FCSTD DOCUMENT  (FreeCAD 1.1R41365 (Git))
Label: MicroManipulatorAssembly
License: All rights reserved
LicenseURL: https://en.wikipedia.org/wiki/All_rights_reserved
objects: App::Link×31, Assembly::AssemblyLink×7, App::Point×5, Assembly::JointGroup×1, Assembly::AssemblyObject×1
EXTERNAL_REF file=ActuatorAssembly.FCStd obj=Assembly
EXTERNAL_REF file=ActuatorAssembly.FCStd obj=FlexureStageBase
EXTERNAL_REF file=ActuatorAssembly.FCStd obj=FlexureStage
EXTERNAL_REF file=EndEffectorAssembly.FCStd obj=Assembly
EXTERNAL_REF file=EndEffectorAssembly.FCStd obj=Endeffector
EXTERNAL_REF file=ActuatorAssembly.FCStd obj=LeadscrewWheel
EXTERNAL_REF file=ActuatorAssembly.FCStd obj=FlexureAssembly
EXTERNAL_REF file=FlexureAssembly.FCStd obj=WireMount
EXTERNAL_REF file=FlexureAssembly.FCStd obj=WireMount001
EXTERNAL_REF file=FlexureAssembly.FCStd obj=FlexureWire
EXTERNAL_REF file=FlexureAssembly.FCStd obj=FlexureWire001
EXTERNAL_REF file=FlexureAssembly.FCStd obj=Rod
EXTERNAL_REF file=FlexureAssembly.FCStd obj=FlexureStiffener
EXTERNAL_REF file=FlexureAssembly.FCStd obj=WireMountFixture

FEATURE [App::Point] Origin001
  Role = Origin
FEATURE [Assembly::JointGroup] Joints
FEATURE [App::Point] Origin003
  Role = Origin
FEATURE [App::Link] FlexureStageBase
  LinkPlacement = pos=(3.75918e-06,-42.5,2) rot=(0,0,1;3.14159rad)
  LinkedObject = -> <external ActuatorAssembly.FCStd>#FlexureStageBase
  Placement = pos=(3.75918e-06,-42.5,2) rot=(0,0,1;3.14159rad)
FEATURE [App::Link] FlexureStage
  LinkPlacement = pos=(0,-19,19) rot=(0,1,0;3.14159rad)
  LinkedObject = -> <external ActuatorAssembly.FCStd>#FlexureStage
  Placement = pos=(0,-19,19) rot=(0,1,0;3.14159rad)
FEATURE [App::Point] Origin005
  Role = Origin
FEATURE [App::Link] FlexureStageBase001
  LinkPlacement = pos=(3.75918e-06,-42.5,2) rot=(0,0,1;3.14159rad)
  LinkedObject = -> <external ActuatorAssembly.FCStd>#FlexureStageBase
  Placement = pos=(3.75918e-06,-42.5,2) rot=(0,0,1;3.14159rad)
FEATURE [App::Link] FlexureStage001
  LinkPlacement = pos=(0,-19,19) rot=(0,1,0;3.14159rad)
  LinkedObject = -> <external ActuatorAssembly.FCStd>#FlexureStage
  Placement = pos=(0,-19,19) rot=(0,1,0;3.14159rad)
FEATURE [App::Point] Origin007
  Role = Origin
FEATURE [App::Link] FlexureStageBase002
  LinkPlacement = pos=(3.75918e-06,-42.5,2) rot=(0,0,1;3.14159rad)
  LinkedObject = -> <external ActuatorAssembly.FCStd>#FlexureStageBase
  Placement = pos=(3.75918e-06,-42.5,2) rot=(0,0,1;3.14159rad)
FEATURE [App::Link] FlexureStage002
  LinkPlacement = pos=(0,-19,19) rot=(0,1,0;3.14159rad)
  LinkedObject = -> <external ActuatorAssembly.FCStd>#FlexureStage
  Placement = pos=(0,-19,19) rot=(0,1,0;3.14159rad)
FEATURE [App::Point] Origin009
  Role = Origin
FEATURE [App::Link] Endeffector
  LinkedObject = -> <external EndEffectorAssembly.FCStd>#Endeffector
FEATURE [Assembly::AssemblyLink] EndEffectorAssembly
  Group = -> [Endeffector]
  LinkedObject = -> <external EndEffectorAssembly.FCStd>#Assembly
  Origin = -> Origin008
  Placement = pos=(0,0,0) rot=(0,0,1;1.5708rad)
  Rigid = true
FEATURE [App::Link] LeadscrewWheel
  LinkPlacement = pos=(23,-13,13) rot=(0,1,0;1.5708rad)
  LinkedObject = -> <external ActuatorAssembly.FCStd>#LeadscrewWheel
  Placement = pos=(23,-13,13) rot=(0,1,0;1.5708rad)
FEATURE [App::Link] LeadscrewWheel001
  LinkPlacement = pos=(23,-13,13) rot=(0,1,0;1.5708rad)
  LinkedObject = -> <external ActuatorAssembly.FCStd>#LeadscrewWheel
  Placement = pos=(23,-13,13) rot=(0,1,0;1.5708rad)
FEATURE [App::Link] LeadscrewWheel002
  LinkPlacement = pos=(23,-13,13) rot=(0,1,0;1.5708rad)
  LinkedObject = -> <external ActuatorAssembly.FCStd>#LeadscrewWheel
  Placement = pos=(23,-13,13) rot=(0,1,0;1.5708rad)
FEATURE [App::Link] WireMount006
  LinkedObject = -> <external FlexureAssembly.FCStd>#WireMount
FEATURE [App::Link] WireMount007
  LinkPlacement = pos=(0,-55,3) rot=(1,0,0;3.14159rad)
  LinkedObject = -> <external FlexureAssembly.FCStd>#WireMount001
  Placement = pos=(0,-55,3) rot=(1,0,0;3.14159rad)
FEATURE [App::Link] FlexureWire006
  LinkPlacement = pos=(8,3.5,1.5) rot=(0,0,1;0rad)
  LinkedObject = -> <external FlexureAssembly.FCStd>#FlexureWire
  Placement = pos=(8,3.5,1.5) rot=(0,0,1;0rad)
FEATURE [App::Link] FlexureWire007
  LinkPlacement = pos=(-8.00001,3.5,1.5) rot=(0,0,1;0rad)
  LinkedObject = -> <external FlexureAssembly.FCStd>#FlexureWire001
  Placement = pos=(-8.00001,3.5,1.5) rot=(0,0,1;0rad)
FEATURE [App::Link] Rod003  label="FlexureStiffener003"
  LinkPlacement = pos=(-8,-27.5,1.5) rot=(0,0,1;0rad)
  LinkedObject = -> <external FlexureAssembly.FCStd>#Rod
  Placement = pos=(-8,-27.5,1.5) rot=(0,0,1;0rad)
FEATURE [App::Link] FlexureStiffener003
  LinkPlacement = pos=(8,-27.5,1.5) rot=(0,0,1;0rad)
  LinkedObject = -> <external FlexureAssembly.FCStd>#FlexureStiffener
  Placement = pos=(8,-27.5,1.5) rot=(0,0,1;0rad)
FEATURE [App::Link] WireMountFixture003
  LinkPlacement = pos=(0,-27.5,-5) rot=(0,0,1;0rad)
  LinkedObject = -> <external FlexureAssembly.FCStd>#WireMountFixture
  Placement = pos=(0,-27.5,-5) rot=(0,0,1;0rad)
FEATURE [Assembly::AssemblyLink] FlexureAssembly003  label="FlexureAssembly"
  Group = -> [WireMount006,WireMount007,FlexureWire006,FlexureWire007,Rod003,FlexureStiffener003,WireMountFixture003]
  LinkedObject = -> <external ActuatorAssembly.FCStd>#FlexureAssembly
  Placement = pos=(-54.5,-13,19) rot=(0,0,1;1.5708rad)
  Rigid = true
FEATURE [Assembly::AssemblyLink] ActuatorAssembly  label="ActuatorAssembly1"
  Group = -> [FlexureStageBase,FlexureStage,LeadscrewWheel,FlexureAssembly003]
  LinkedObject = -> <external ActuatorAssembly.FCStd>#Assembly
  Origin = -> Origin002
  Placement = pos=(51.5,14.5,-33.5) rot=(-0.660516,-0.330258,0.674276;0rad)
  Rigid = true
FEATURE [App::Link] WireMount008
  LinkedObject = -> <external FlexureAssembly.FCStd>#WireMount
FEATURE [App::Link] WireMount009
  LinkPlacement = pos=(0,-55,3) rot=(1,0,0;3.14159rad)
  LinkedObject = -> <external FlexureAssembly.FCStd>#WireMount001
  Placement = pos=(0,-55,3) rot=(1,0,0;3.14159rad)
FEATURE [App::Link] FlexureWire008
  LinkPlacement = pos=(8,3.5,1.5) rot=(0,0,1;0rad)
  LinkedObject = -> <external FlexureAssembly.FCStd>#FlexureWire
  Placement = pos=(8,3.5,1.5) rot=(0,0,1;0rad)
FEATURE [App::Link] FlexureWire009
  LinkPlacement = pos=(-8.00001,3.5,1.5) rot=(0,0,1;0rad)
  LinkedObject = -> <external FlexureAssembly.FCStd>#FlexureWire001
  Placement = pos=(-8.00001,3.5,1.5) rot=(0,0,1;0rad)
FEATURE [App::Link] Rod004  label="FlexureStiffener004"
  LinkPlacement = pos=(-8,-27.5,1.5) rot=(0,0,1;0rad)
  LinkedObject = -> <external FlexureAssembly.FCStd>#Rod
  Placement = pos=(-8,-27.5,1.5) rot=(0,0,1;0rad)
FEATURE [App::Link] FlexureStiffener004
  LinkPlacement = pos=(8,-27.5,1.5) rot=(0,0,1;0rad)
  LinkedObject = -> <external FlexureAssembly.FCStd>#FlexureStiffener
  Placement = pos=(8,-27.5,1.5) rot=(0,0,1;0rad)
FEATURE [App::Link] WireMountFixture004
  LinkPlacement = pos=(0,-27.5,-5) rot=(0,0,1;0rad)
  LinkedObject = -> <external FlexureAssembly.FCStd>#WireMountFixture
  Placement = pos=(0,-27.5,-5) rot=(0,0,1;0rad)
FEATURE [Assembly::AssemblyLink] FlexureAssembly004
  Group = -> [WireMount008,WireMount009,FlexureWire008,FlexureWire009,Rod004,FlexureStiffener004,WireMountFixture004]
  LinkedObject = -> <external ActuatorAssembly.FCStd>#FlexureAssembly
  Placement = pos=(-54.5,-13,19) rot=(0,0,1;1.5708rad)
  Rigid = true
FEATURE [Assembly::AssemblyLink] ActuatorAssembly001  label="ActuatorAssembly2"
  Group = -> [FlexureStageBase001,FlexureStage001,LeadscrewWheel001,FlexureAssembly004]
  LinkedObject = -> <external ActuatorAssembly.FCStd>#Assembly
  Origin = -> Origin004
  Placement = pos=(33.5,-51.5,14.5) rot=(-0.57735,0.57735,0.57735;4.18879rad)
  Rigid = true
FEATURE [App::Link] WireMount010
  LinkedObject = -> <external FlexureAssembly.FCStd>#WireMount
FEATURE [App::Link] WireMount011
  LinkPlacement = pos=(0,-55,3) rot=(1,0,0;3.14159rad)
  LinkedObject = -> <external FlexureAssembly.FCStd>#WireMount001
  Placement = pos=(0,-55,3) rot=(1,0,0;3.14159rad)
FEATURE [App::Link] FlexureWire010
  LinkPlacement = pos=(8,3.5,1.5) rot=(0,0,1;0rad)
  LinkedObject = -> <external FlexureAssembly.FCStd>#FlexureWire
  Placement = pos=(8,3.5,1.5) rot=(0,0,1;0rad)
FEATURE [App::Link] FlexureWire011
  LinkPlacement = pos=(-8.00001,3.5,1.5) rot=(0,0,1;0rad)
  LinkedObject = -> <external FlexureAssembly.FCStd>#FlexureWire001
  Placement = pos=(-8.00001,3.5,1.5) rot=(0,0,1;0rad)
FEATURE [App::Link] Rod005  label="FlexureStiffener005"
  LinkPlacement = pos=(-8,-27.5,1.5) rot=(0,0,1;0rad)
  LinkedObject = -> <external FlexureAssembly.FCStd>#Rod
  Placement = pos=(-8,-27.5,1.5) rot=(0,0,1;0rad)
FEATURE [App::Link] FlexureStiffener005
  LinkPlacement = pos=(8,-27.5,1.5) rot=(0,0,1;0rad)
  LinkedObject = -> <external FlexureAssembly.FCStd>#FlexureStiffener
  Placement = pos=(8,-27.5,1.5) rot=(0,0,1;0rad)
FEATURE [App::Link] WireMountFixture005
  LinkPlacement = pos=(0,-27.5,-5) rot=(0,0,1;0rad)
  LinkedObject = -> <external FlexureAssembly.FCStd>#WireMountFixture
  Placement = pos=(0,-27.5,-5) rot=(0,0,1;0rad)
FEATURE [Assembly::AssemblyLink] FlexureAssembly005
  Group = -> [WireMount010,WireMount011,FlexureWire010,FlexureWire011,Rod005,FlexureStiffener005,WireMountFixture005]
  LinkedObject = -> <external ActuatorAssembly.FCStd>#FlexureAssembly
  Placement = pos=(-54.5,-13,19) rot=(0,0,1;1.5708rad)
  Rigid = true
FEATURE [Assembly::AssemblyLink] ActuatorAssembly002  label="ActuatorAssembly3"
  Group = -> [FlexureStageBase002,FlexureStage002,LeadscrewWheel002,FlexureAssembly005]
  LinkedObject = -> <external ActuatorAssembly.FCStd>#Assembly
  Origin = -> Origin006
  Placement = pos=(-14.5,-33.5,-51.5) rot=(-0.57735,0.57735,0.57735;2.0944rad)
  Rigid = true
FEATURE [Assembly::AssemblyObject] Assembly  label="MicroManipulator"
  Group = -> [Joints,ActuatorAssembly,ActuatorAssembly001,ActuatorAssembly002,EndEffectorAssembly]
  Origin = -> Origin
  Type = Assembly

RESOLVED EXTERNAL PARTS (link-assembly join: the EXTERNAL_REF files above that resolve inside this repo's crawl, each included once):
---- part ActuatorAssembly.FCStd = doc fcstd_1e1ebc22bf72 ----
FCSTD DOCUMENT  (FreeCAD 1.1R41365 (Git))
Label: ActuatorAssembly
License: All rights reserved
LicenseURL: https://en.wikipedia.org/wiki/All_rights_reserved
objects: App::Link×10, App::Point×2, App::FeaturePython×1, Assembly::JointGroup×1, Assembly::AssemblyLink×1, Assembly::AssemblyObject×1
EXTERNAL_REF file=FlexureStageBase.FCStd obj=Body
EXTERNAL_REF file=FlexureStage.FCStd obj=Body
EXTERNAL_REF file=LeadscrewWheel.FCStd obj=Body
EXTERNAL_REF file=FlexureAssembly.FCStd obj=Assembly
EXTERNAL_REF file=FlexureAssembly.FCStd obj=WireMount
EXTERNAL_REF file=FlexureAssembly.FCStd obj=WireMount001
EXTERNAL_REF file=FlexureAssembly.FCStd obj=FlexureWire
EXTERNAL_REF file=FlexureAssembly.FCStd obj=FlexureWire001
EXTERNAL_REF file=FlexureAssembly.FCStd obj=Rod
EXTERNAL_REF file=FlexureAssembly.FCStd obj=FlexureStiffener
EXTERNAL_REF file=FlexureAssembly.FCStd obj=WireMountFixture

FEATURE [App::Point] Origin001
  Role = Origin
FEATURE [App::Link] FlexureStageBase
  LinkPlacement = pos=(3.75918e-06,-42.5,2) rot=(0,0,1;3.14159rad)
  LinkedObject = -> <external FlexureStageBase.FCStd>#Body
  Placement = pos=(3.75918e-06,-42.5,2) rot=(0,0,1;3.14159rad)
FEATURE [App::Link] FlexureStage
  LinkPlacement = pos=(0,-19,19) rot=(0,1,0;3.14159rad)
  LinkedObject = -> <external FlexureStage.FCStd>#Body
  Placement = pos=(0,-19,19) rot=(0,1,0;3.14159rad)
FEATURE [App::Link] LeadscrewWheel
  LinkPlacement = pos=(23,-13,13) rot=(0,1,0;1.5708rad)
  LinkedObject = -> <external LeadscrewWheel.FCStd>#Body
  Placement = pos=(23,-13,13) rot=(0,1,0;1.5708rad)
FEATURE [App::FeaturePython] GroundedJoint  # Assembly grounded joint (typed FeaturePython)
  ObjectToGround = -> LeadscrewWheel
FEATURE [Assembly::JointGroup] Joints
  Group = -> [GroundedJoint]
FEATURE [App::Point] Origin003
  Role = Origin
FEATURE [App::Link] WireMount  label="WireMount1"
  LinkedObject = -> <external FlexureAssembly.FCStd>#WireMount
FEATURE [App::Link] WireMount001  label="WireMount2"
  LinkPlacement = pos=(0,-55,3) rot=(1,0,0;3.14159rad)
  LinkedObject = -> <external FlexureAssembly.FCStd>#WireMount001
  Placement = pos=(0,-55,3) rot=(1,0,0;3.14159rad)
FEATURE [App::Link] FlexureWire  label="FlexureWire1"
  LinkPlacement = pos=(8,3.5,1.5) rot=(0,0,1;0rad)
  LinkedObject = -> <external FlexureAssembly.FCStd>#FlexureWire
  Placement = pos=(8,3.5,1.5) rot=(0,0,1;0rad)
FEATURE [App::Link] FlexureWire001  label="FlexureWire2"
  LinkPlacement = pos=(-8.00001,3.5,1.5) rot=(0,0,1;0rad)
  LinkedObject = -> <external FlexureAssembly.FCStd>#FlexureWire001
  Placement = pos=(-8.00001,3.5,1.5) rot=(0,0,1;0rad)
FEATURE [App::Link] Rod  label="FlexureStiffener1"
  LinkPlacement = pos=(-8,-27.5,1.5) rot=(0,0,1;0rad)
  LinkedObject = -> <external FlexureAssembly.FCStd>#Rod
  Placement = pos=(-8,-27.5,1.5) rot=(0,0,1;0rad)
FEATURE [App::Link] FlexureStiffener  label="FlexureStiffener2"
  LinkPlacement = pos=(8,-27.5,1.5) rot=(0,0,1;0rad)
  LinkedObject = -> <external FlexureAssembly.FCStd>#FlexureStiffener
  Placement = pos=(8,-27.5,1.5) rot=(0,0,1;0rad)
FEATURE [App::Link] WireMountFixture
  LinkPlacement = pos=(0,-27.5,-5) rot=(0,0,1;0rad)
  LinkedObject = -> <external FlexureAssembly.FCStd>#WireMountFixture
  Placement = pos=(0,-27.5,-5) rot=(0,0,1;0rad)
FEATURE [Assembly::AssemblyLink] FlexureAssembly
  Group = -> [WireMount,WireMount001,FlexureWire,FlexureWire001,Rod,FlexureStiffener,WireMountFixture]
  LinkedObject = -> <external FlexureAssembly.FCStd>#Assembly
  Origin = -> Origin002
  Placement = pos=(-54.5,-13,22) rot=(0.707107,-0.707107,0;3.14159rad)
  Rigid = true
FEATURE [Assembly::AssemblyObject] Assembly  label="ActuatorAssembly"
  Group = -> [Joints,FlexureStageBase,FlexureStage,LeadscrewWheel,GroundedJoint,FlexureAssembly]
  Origin = -> Origin
  Type = Assembly
---- part FlexureAssembly.FCStd = doc fcstd_80823ab9bab4 ----
FCSTD DOCUMENT  (FreeCAD 1.1R41365 (Git))
Label: FlexureAssembly
License: All rights reserved
LicenseURL: https://en.wikipedia.org/wiki/All_rights_reserved
objects: App::Link×7, App::Point×1, App::FeaturePython×1, Assembly::JointGroup×1, Assembly::AssemblyObject×1
EXTERNAL_REF file=WireMount.FCStd obj=Body
EXTERNAL_REF file=FlexureWire.FCStd obj=Body
EXTERNAL_REF file=FlexureStiffener.FCStd obj=Body
EXTERNAL_REF file=WireMountFixture.FCStd obj=Body

FEATURE [App::Point] Origin001
  Role = Origin
FEATURE [App::Link] WireMount  label="WireMount1"
  LinkedObject = -> <external WireMount.FCStd>#Body
FEATURE [App::FeaturePython] GroundedJoint  # Assembly grounded joint (typed FeaturePython)
  ObjectToGround = -> WireMount
FEATURE [Assembly::JointGroup] Joints
  Group = -> [GroundedJoint]
FEATURE [App::Link] WireMount001  label="WireMount2"
  LinkPlacement = pos=(0,-55,3) rot=(1,0,0;3.14159rad)
  LinkedObject = -> <external WireMount.FCStd>#Body
  Placement = pos=(0,-55,3) rot=(1,0,0;3.14159rad)
FEATURE [App::Link] FlexureWire  label="FlexureWire1"
  LinkPlacement = pos=(8,3.5,1.5) rot=(0,0,1;0rad)
  LinkedObject = -> <external FlexureWire.FCStd>#Body
  Placement = pos=(8,3.5,1.5) rot=(0,0,1;0rad)
FEATURE [App::Link] FlexureWire001  label="FlexureWire2"
  LinkPlacement = pos=(-8.00001,3.5,1.5) rot=(0,0,1;0rad)
  LinkedObject = -> <external FlexureWire.FCStd>#Body
  Placement = pos=(-8.00001,3.5,1.5) rot=(0,0,1;0rad)
FEATURE [App::Link] Rod  label="FlexureStiffener1"
  LinkPlacement = pos=(-8,-27.5,1.5) rot=(0,0,1;0rad)
  LinkedObject = -> <external FlexureStiffener.FCStd>#Body
  Placement = pos=(-8,-27.5,1.5) rot=(0,0,1;0rad)
FEATURE [App::Link] FlexureStiffener  label="FlexureStiffener2"
  LinkPlacement = pos=(8,-27.5,1.5) rot=(0,0,1;0rad)
  LinkedObject = -> <external FlexureStiffener.FCStd>#Body
  Placement = pos=(8,-27.5,1.5) rot=(0,0,1;0rad)
FEATURE [App::Link] WireMountFixture
  LinkPlacement = pos=(0,-27.5,-5) rot=(0,0,1;0rad)
  LinkedObject = -> <external WireMountFixture.FCStd>#Body
  Placement = pos=(0,-27.5,-5) rot=(0,0,1;0rad)
FEATURE [Assembly::AssemblyObject] Assembly  label="FlexureAssembly"
  Group = -> [Joints,WireMount,GroundedJoint,WireMount001,FlexureWire,FlexureWire001,Rod,FlexureStiffener,WireMountFixture]
  Origin = -> Origin
  Type = Assembly
